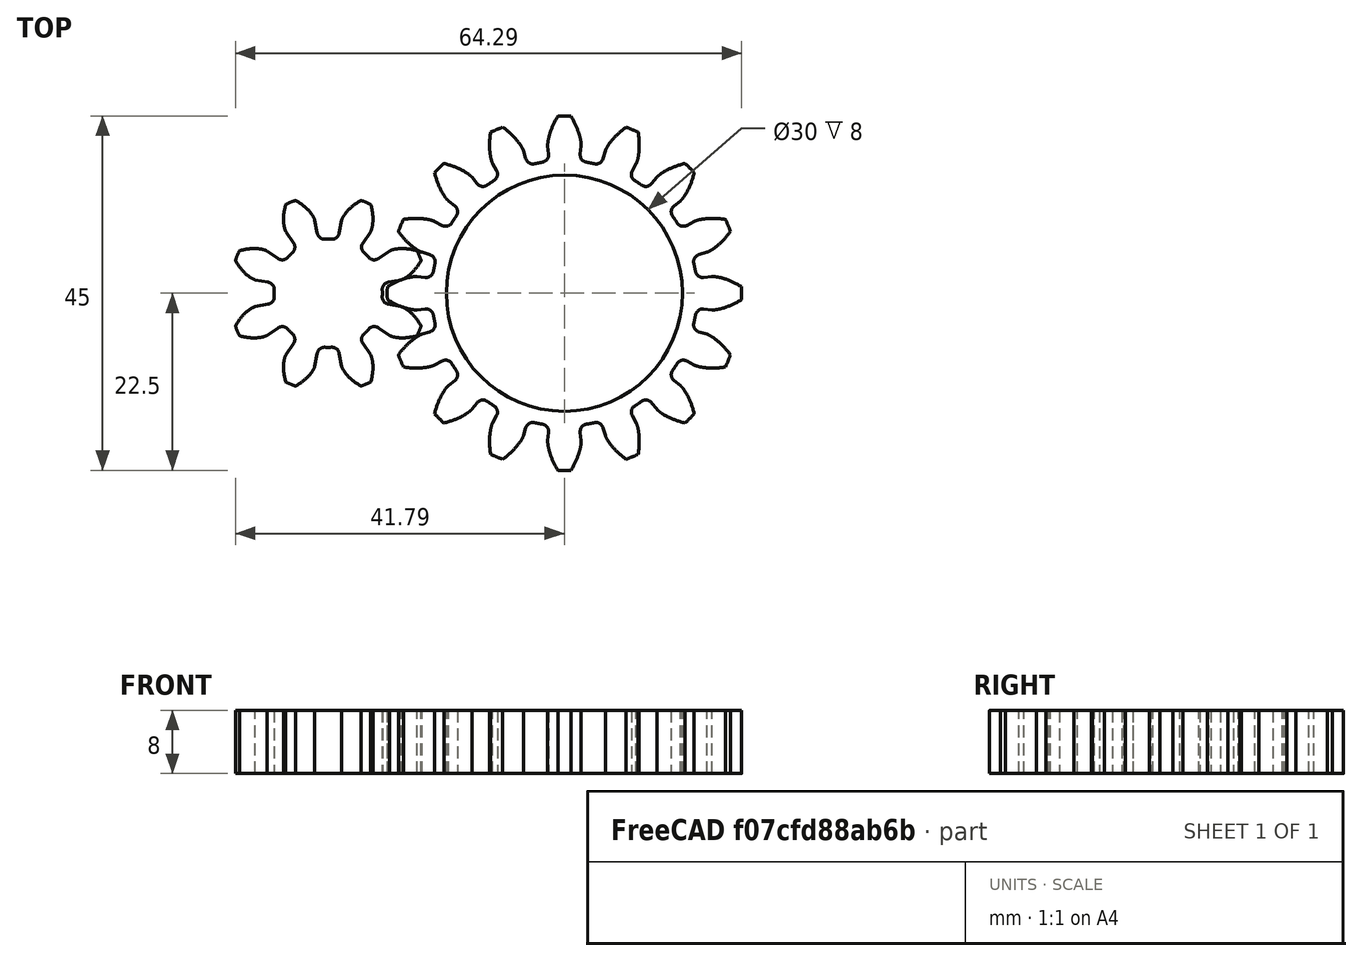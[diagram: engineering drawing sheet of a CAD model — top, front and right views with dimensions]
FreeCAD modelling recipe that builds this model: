
FCSTD DOCUMENT  (FreeCAD 0.18R16146 (Git))
Label: Gears
License: All rights reserved
LicenseURL: http://en.wikipedia.org/wiki/All_rights_reserved
objects: Part::Part2DObjectPython×2, Part::Extrusion×2, Part::Cylinder×1, Part::Cut×1
note: 6 computed .brp shape members not serialized (recipe doc carries the construction recipe); baked Part::Feature solids carry a one-line shape summary decoded from their .brp

FEATURE [Part::Part2DObjectPython] InvoluteGear  # Draft 2D object (typed FeaturePython)
  ExternalGear = true
  HighPrecision = true
  Modules = 2.5
  NumberOfTeeth = 16
  PressureAngle = 20
FEATURE [Part::Extrusion] Extrude
  Base = -> InvoluteGear
  Dir = (0,0,1)
  DirMode = 2
  FaceMakerClass = Part::FaceMakerBullseye
  LengthFwd = 8
  LengthRev = 0
  Solid = true
  Symmetric = false
FEATURE [Part::Cylinder] Cylinder
  Angle = 360
  AttacherType = Attacher::AttachEngine3D
  Height = 10
  Radius = 15
FEATURE [Part::Cut] Cut
  Base = -> Extrude
  Tool = -> Cylinder
FEATURE [Part::Part2DObjectPython] InvoluteGear001  # Draft 2D object (typed FeaturePython)
  ExternalGear = true
  HighPrecision = true
  Modules = 2.5
  NumberOfTeeth = 8
  PressureAngle = 20
FEATURE [Part::Extrusion] Extrude001
  Base = -> InvoluteGear001
  Dir = (0,0,1)
  DirMode = 2
  FaceMakerClass = Part::FaceMakerBullseye
  LengthFwd = 8
  LengthRev = 0
  Placement = pos=(-30,0,0) rot=(0,0,1;0.392699rad)
  Solid = true
  Symmetric = false
